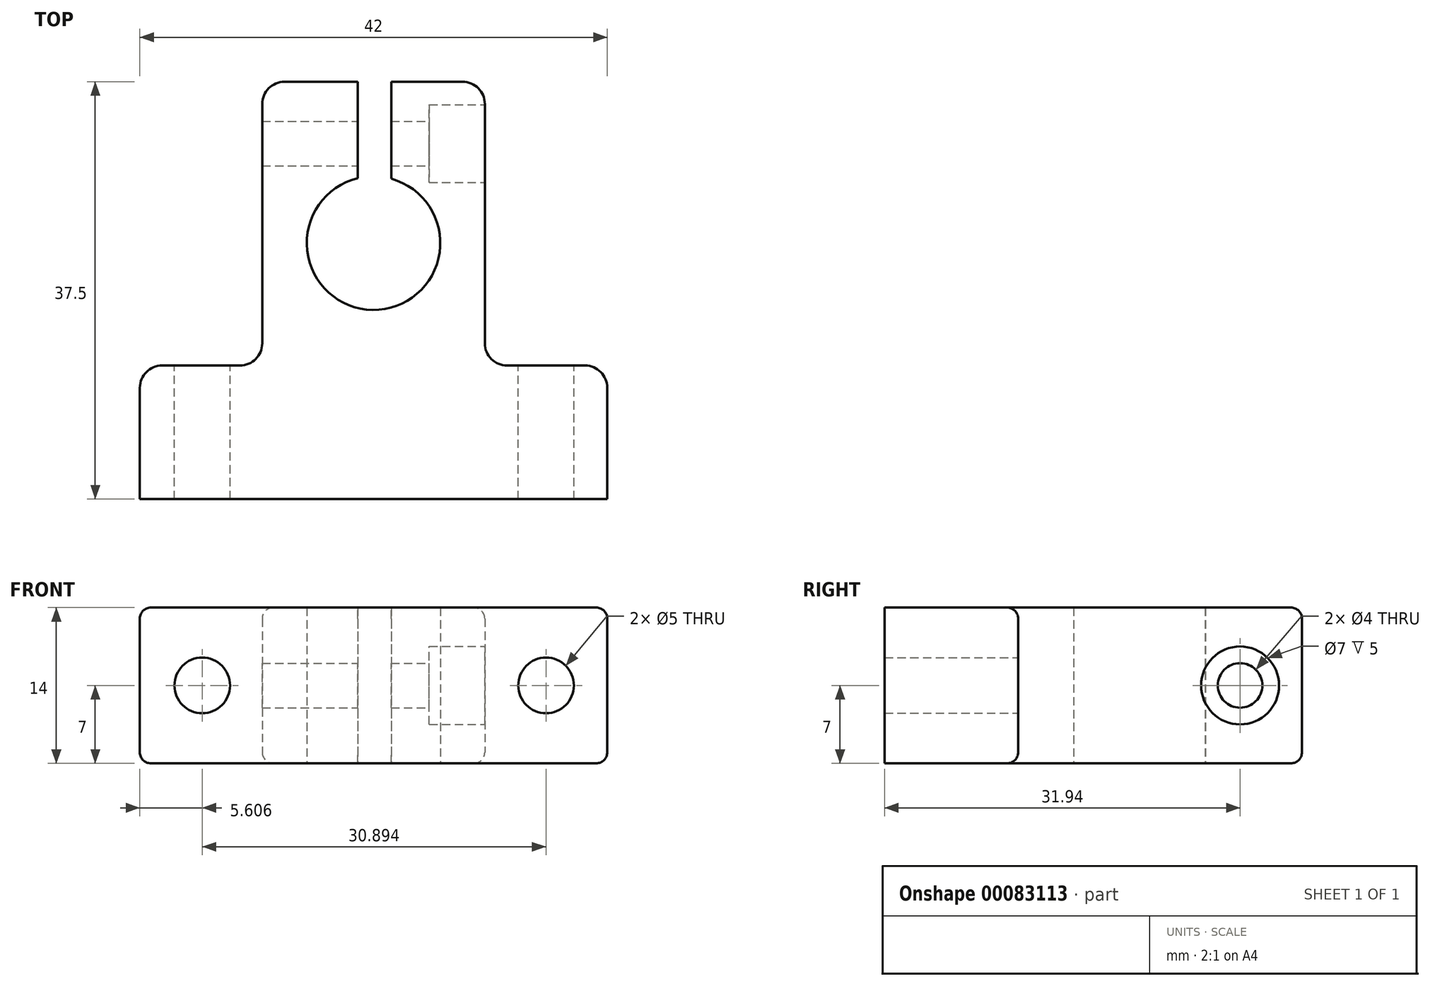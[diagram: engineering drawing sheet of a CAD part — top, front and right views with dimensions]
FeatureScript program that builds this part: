
annotation { "Feature Type Name" : "Feature", "Feature Type Description" : "" }
export const myFeature = defineFeature(function(context is Context, id is Id, definition is map)
    precondition{}
    {
        {
            var Q0;
            Q0=qCreatedBy(makeId("Top.planeOp"),FACE);
            var sketch = newSketch(context, id + "F0", { "sketchPlane" : qUnion([Q0])});
            skLineSegment(sketch, "E0", {"start": v(-75.16, -74.59) * mm, "end": v(-33.16, -74.59) * mm});
            skLineSegment(sketch, "E1", {"start": v(-33.16, -74.59) * mm, "end": v(-33.16, -64.59) * mm});
            skLineSegment(sketch, "E2", {"start": v(-35.16, -62.59) * mm, "end": v(-42.16, -62.59) * mm});
            skLineSegment(sketch, "E3", {"start": v(-44.16, -60.59) * mm, "end": v(-44.16, -39.09) * mm});
            skLineSegment(sketch, "E4", {"start": v(-46.16, -37.09) * mm, "end": v(-62.16, -37.09) * mm});
            skLineSegment(sketch, "E5", {"start": v(-64.16, -39.09) * mm, "end": v(-64.16, -60.59) * mm});
            skLineSegment(sketch, "E6", {"start": v(-66.16, -62.59) * mm, "end": v(-73.16, -62.59) * mm});
            skLineSegment(sketch, "E7", {"start": v(-75.16, -64.59) * mm, "end": v(-75.16, -74.59) * mm});
            skCircle(sketch, "E8", {"center": v(-54.16, -51.59) * mm, "radius": 6 * mm});
            skLineSegment(sketch, "E9", {"start": v(-54.16, -37.09) * mm, "end": v(-55.57, -37.09) * mm});
            skLineSegment(sketch, "E10.bottom", {"start": v(-55.57, -37.09) * mm, "end": v(-52.57, -37.09) * mm});
            skLineSegment(sketch, "E10.top", {"start": v(-55.57, -45.8) * mm, "end": v(-52.57, -45.8) * mm});
            skLineSegment(sketch, "E10.left", {"start": v(-55.57, -37.09) * mm, "end": v(-55.57, -45.8) * mm});
            skLineSegment(sketch, "E10.right", {"start": v(-52.57, -37.09) * mm, "end": v(-52.57, -45.8) * mm});
            skPoint(sketch, "E11.visualSharp", {"position": v(-64.16, -62.59) * mm});
            skArc(sketch, "E11.filletArc", {"start": v(-66.16, -62.59) * mm, "mid": v(-64.75, -62) * mm, "end": v(-64.16, -60.59) * mm});
            skPoint(sketch, "E12.visualSharp", {"position": v(-44.16, -62.59) * mm});
            skArc(sketch, "E12.filletArc", {"start": v(-44.16, -60.59) * mm, "mid": v(-43.57, -62) * mm, "end": v(-42.16, -62.59) * mm});
            skPoint(sketch, "E13.visualSharp", {"position": v(-64.16, -37.09) * mm});
            skArc(sketch, "E13.filletArc", {"start": v(-62.16, -37.09) * mm, "mid": v(-63.57, -37.68) * mm, "end": v(-64.16, -39.09) * mm});
            skPoint(sketch, "E14.visualSharp", {"position": v(-44.16, -37.09) * mm});
            skArc(sketch, "E14.filletArc", {"start": v(-44.16, -39.09) * mm, "mid": v(-44.75, -37.68) * mm, "end": v(-46.16, -37.09) * mm});
            skPoint(sketch, "E15.visualSharp", {"position": v(-75.16, -62.59) * mm});
            skArc(sketch, "E15.filletArc", {"start": v(-73.16, -62.59) * mm, "mid": v(-74.57, -63.18) * mm, "end": v(-75.16, -64.59) * mm});
            skPoint(sketch, "E16.visualSharp", {"position": v(-33.16, -62.59) * mm});
            skArc(sketch, "E16.filletArc", {"start": v(-33.16, -64.59) * mm, "mid": v(-33.75, -63.18) * mm, "end": v(-35.16, -62.59) * mm});
            skSolve(sketch);
        }
        {
            var Q0;
            Q0=makeQuery(id+"F0.imprint","IMPRINT",FACE,{"disambiguationData":[TD([[makeQuery(id+"F0.imprint","IMPRINT",EDGE,{"derivedFrom":sQuery(id+"F0.wireOp",EDGE,"E0")}),1.0]])]});
            extrude(context, id + "F1", {"entities" : qUnion([Q0]), "depth" : 14 * mm});
        }
        {
            var Q0;
            Q0=makeQuery(id+"F1.opExtrude","SWEPT_FACE",FACE,{"disambiguationData":[OSD([sQuery(id+"F0.wireOp",EDGE,"E3")])]});
            var sketch = newSketch(context, id + "F2", { "sketchPlane" : qUnion([Q0])});
            skCircle(sketch, "E17", {"center": v(-42.65, 7) * mm, "radius": 2 * mm});
            skPoint(sketch, "E17.centerSnap0", {"position": v(-39.09, 7) * mm});
            skCircle(sketch, "E18", {"center": v(-42.65, 7) * mm, "radius": 3.5 * mm});
            skSolve(sketch);
        }
        {
            var Q0;
            Q0=makeQuery(id+"F2.imprint","IMPRINT",FACE,{"disambiguationData":[TD([[makeQuery(id+"F2.imprint","IMPRINT",EDGE,{"derivedFrom":sQuery(id+"F2.wireOp",EDGE,"E17")}),-1.0]])]});
            extrude(context, id + "F3", {"entities" : qUnion([Q0]), "operationType" : NewBodyOperationType.REMOVE, "oppositeDirection" : true, "depth" : 5 * mm});
        }
        {
            var Q0;
            Q0=makeQuery(id+"F3.boolean.opBoolean","SPLIT",FACE,{"disambiguationData":[TD([makeQuery(id+"F3.opExtrude","SWEPT_FACE",FACE,{"disambiguationData":[OSD([sQuery(id+"F2.wireOp",EDGE,"E17")])]})])],"derivedFrom":makeQuery(id+"F1.opExtrude","SWEPT_FACE",FACE,{"disambiguationData":[OSD([sQuery(id+"F0.wireOp",EDGE,"E3")])]})});
            extrude(context, id + "F4", {"entities" : qUnion([Q0]), "operationType" : NewBodyOperationType.REMOVE, "oppositeDirection" : true, "depth" : 25 * mm});
        }
        {
            var Q0;
            Q0=makeQuery(id+"F1.opExtrude","SWEPT_FACE",FACE,{"disambiguationData":[OSD([sQuery(id+"F0.wireOp",EDGE,"E2")])]});
            var sketch = newSketch(context, id + "F5", { "sketchPlane" : qUnion([Q0])});
            skCircle(sketch, "E19", {"center": v(38.66, 7) * mm, "radius": 2.5 * mm});
            skPoint(sketch, "E19.centerSnap0", {"position": v(35.16, 7) * mm});
            skPoint(sketch, "E19.centerSnap1", {"position": v(38.66, 14) * mm});
            skCircle(sketch, "E20", {"center": v(69.55, 7) * mm, "radius": 2.5 * mm});
            skSolve(sketch);
        }
        {
            var Q0;
            Q0=makeQuery(id+"F5.imprint","IMPRINT",FACE,{"disambiguationData":[TD([[makeQuery(id+"F5.imprint","IMPRINT",EDGE,{"derivedFrom":sQuery(id+"F5.wireOp",EDGE,"E19")}),1.0]])]});
            var Q1;
            Q1=makeQuery(id+"F5.imprint","IMPRINT",FACE,{"disambiguationData":[TD([[makeQuery(id+"F5.imprint","IMPRINT",EDGE,{"derivedFrom":sQuery(id+"F5.wireOp",EDGE,"E20")}),1.0]])]});
            extrude(context, id + "F6", {"entities" : qUnion([Q0, Q1]), "operationType" : NewBodyOperationType.REMOVE, "oppositeDirection" : true, "depth" : 25 * mm});
        }
        {
            var Q0;
            Q0=makeQuery(id+"F1.opExtrude","CAP_EDGE",EDGE,{"disambiguationData":[OSD([sQuery(id+"F0.wireOp",EDGE,"E3")])],"isStart":false});
            var Q1;
            Q1=makeQuery(id+"F1.opExtrude","CAP_EDGE",EDGE,{"disambiguationData":[OSD([sQuery(id+"F0.wireOp",EDGE,"E5")])],"isStart":false});
            var Q2;
            Q2=makeQuery(id+"F1.opExtrude","CAP_EDGE",EDGE,{"disambiguationData":[OSD([sQuery(id+"F0.wireOp",EDGE,"E3")])],"isStart":true});
            var Q3;
            Q3=makeQuery(id+"F1.opExtrude","CAP_EDGE",EDGE,{"disambiguationData":[OSD([sQuery(id+"F0.wireOp",EDGE,"E5")])],"isStart":true});
            fillet(context, id + "F7", {"entities" : qUnion([Q0, Q1, Q2, Q3]), "radius" : 1 * mm, "tangentPropagation" : true, "allowEdgeOverflow" : false});
        }
    });
